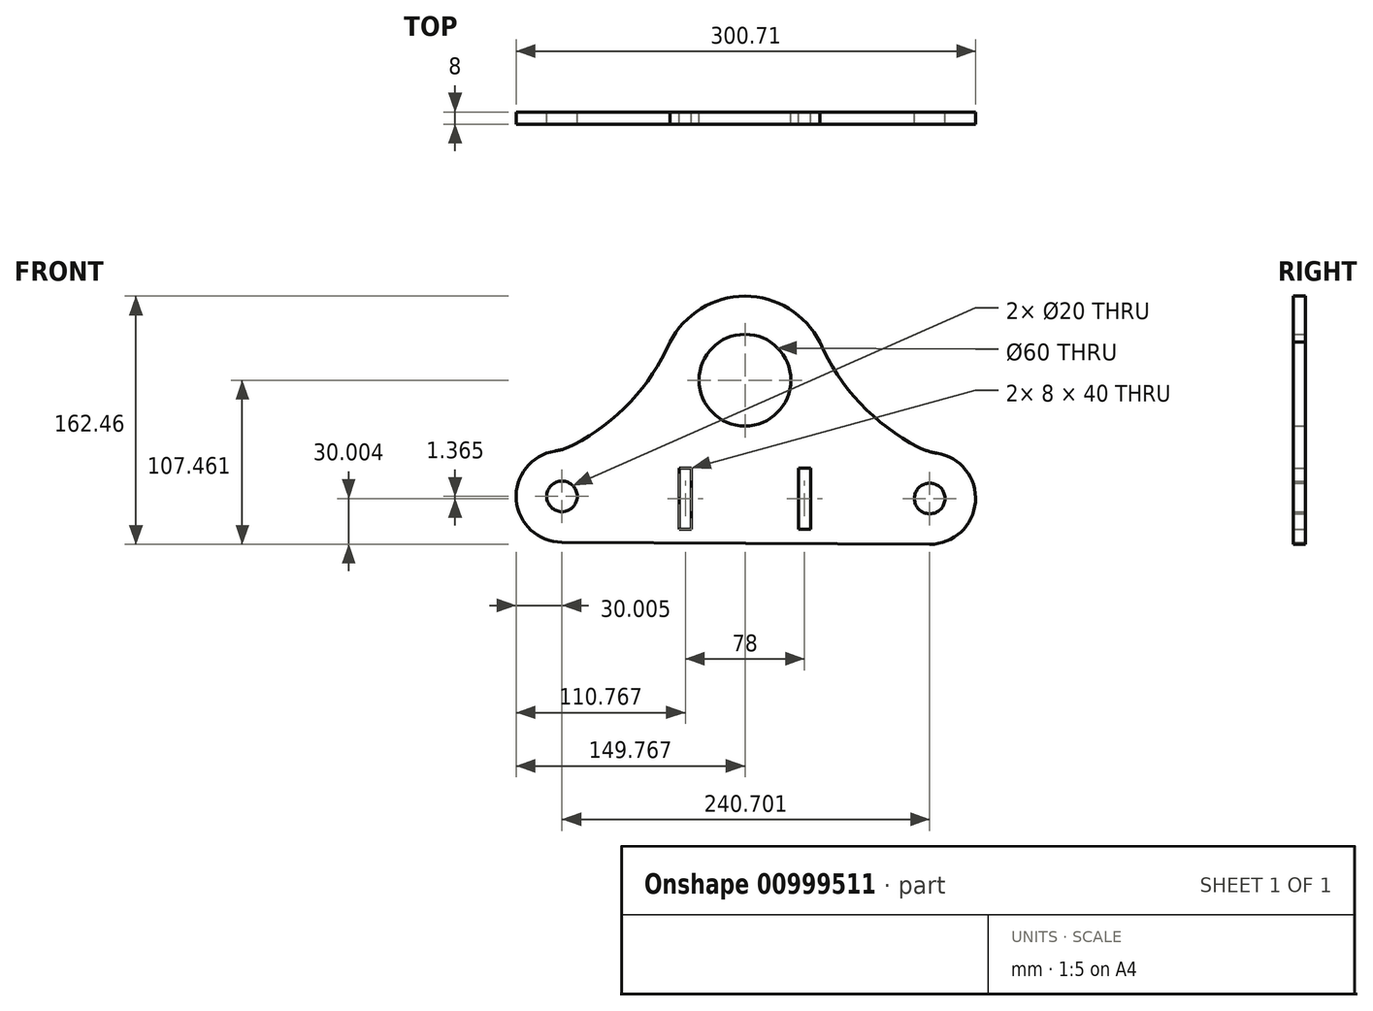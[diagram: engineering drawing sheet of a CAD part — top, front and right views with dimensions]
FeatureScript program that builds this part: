
annotation { "Feature Type Name" : "Feature", "Feature Type Description" : "" }
export const myFeature = defineFeature(function(context is Context, id is Id, definition is map)
    precondition{}
    {
        {
            var Q0;
            Q0=qCreatedBy(makeId("Front.planeOp"),FACE);
            var sketch = newSketch(context, id + "F0", { "sketchPlane" : qUnion([Q0])});
            skLineSegment(sketch, "E0", {"start": v(161.88, -50.78) * mm, "end": v(161.88, 59.22) * mm, "construction": true});
            skLineSegment(sketch, "E1", {"start": v(161.88, 59.22) * mm, "end": v(31.1, 109.22) * mm, "construction": true});
            skLineSegment(sketch, "E2", {"start": v(31.1, 109.22) * mm, "end": v(-27.49, 109.22) * mm, "construction": true});
            skLineSegment(sketch, "E3", {"start": v(-27.49, 109.22) * mm, "end": v(-158.83, 60.74) * mm, "construction": true});
            skLineSegment(sketch, "E4", {"start": v(-158.83, 60.74) * mm, "end": v(-158.83, -49.26) * mm, "construction": true});
            skCircle(sketch, "E5", {"center": v(0.94, 54.22) * mm, "radius": 30 * mm});
            skPoint(sketch, "E5.centerSnap0", {"position": v(0.94, -53.24) * mm});
            skCircle(sketch, "E6", {"center": v(121.88, -23.24) * mm, "radius": 10 * mm});
            skCircle(sketch, "E7", {"center": v(-118.83, -21.87) * mm, "radius": 10 * mm});
            skLineSegment(sketch, "E8.bottom", {"start": v(43.94, -3.24) * mm, "end": v(35.94, -3.24) * mm});
            skLineSegment(sketch, "E8.top", {"start": v(43.94, -43.24) * mm, "end": v(35.94, -43.24) * mm});
            skLineSegment(sketch, "E8.left", {"start": v(43.94, -3.24) * mm, "end": v(43.94, -43.24) * mm});
            skLineSegment(sketch, "E8.right", {"start": v(35.94, -3.24) * mm, "end": v(35.94, -43.24) * mm});
            skLineSegment(sketch, "E9.bottom", {"start": v(-34.06, -3.24) * mm, "end": v(-42.06, -3.24) * mm});
            skLineSegment(sketch, "E9.top", {"start": v(-34.06, -43.24) * mm, "end": v(-42.06, -43.24) * mm});
            skLineSegment(sketch, "E9.left", {"start": v(-34.06, -3.24) * mm, "end": v(-34.06, -43.24) * mm});
            skLineSegment(sketch, "E9.right", {"start": v(-42.06, -3.24) * mm, "end": v(-42.06, -43.24) * mm});
            skCircle(sketch, "E10", {"center": v(-118.83, -21.87) * mm, "radius": 30 * mm});
            skCircle(sketch, "E11", {"center": v(121.88, -23.24) * mm, "radius": 30 * mm});
            skCircle(sketch, "E12", {"center": v(0.94, 54.22) * mm, "radius": 55 * mm});
            skArc(sketch, "E13", {"start": v(-118.83, 8.13) * mm, "mid": v(-76.94, 37.04) * mm, "end": v(-48.15, 79.02) * mm});
            skArc(sketch, "E14", {"start": v(50.03, 79.02) * mm, "mid": v(79.14, 36.12) * mm, "end": v(121.88, 6.76) * mm});
            skLineSegment(sketch, "E15", {"start": v(-118.83, -51.87) * mm, "end": v(121.88, -53.24) * mm});
            skSolve(sketch);
        }
        {
            var Q0;
            Q0=makeQuery(id+"F0.imprint","IMPRINT",FACE,{"disambiguationData":[TD([[makeQuery(id+"F0.imprint","IMPRINT",EDGE,{"derivedFrom":sQuery(id+"F0.wireOp",EDGE,"E7")}),-1.0]])]});
            var Q1;
            Q1=makeQuery(id+"F0.imprint","IMPRINT",FACE,{"disambiguationData":[TD([[makeQuery(id+"F0.imprint","IMPRINT",EDGE,{"derivedFrom":sQuery(id+"F0.wireOp",EDGE,"E8.bottom")}),-1.0]])]});
            var Q2;
            Q2=makeQuery(id+"F0.imprint","IMPRINT",FACE,{"disambiguationData":[TD([[makeQuery(id+"F0.imprint","IMPRINT",EDGE,{"derivedFrom":sQuery(id+"F0.wireOp",EDGE,"E5")}),-1.0]])]});
            var Q3;
            Q3=makeQuery(id+"F0.imprint","IMPRINT",FACE,{"disambiguationData":[TD([[makeQuery(id+"F0.imprint","IMPRINT",EDGE,{"derivedFrom":sQuery(id+"F0.wireOp",EDGE,"E6")}),-1.0]])]});
            extrude(context, id + "F1", {"entities" : qUnion([Q0, Q1, Q2, Q3]), "depth" : 8 * mm, "offsetDistance" : 25 * mm});
        }
        {
            var Q0;
            Q0=makeQuery(id+"F1.opExtrude","SWEPT_EDGE",EDGE,{"disambiguationData":[OSD([sQuery(id+"F0.wireOp",EDGE,"E10"),sQuery(id+"F0.wireOp",EDGE,"E13")])]});
            var Q1;
            Q1=makeQuery(id+"F1.opExtrude","SWEPT_EDGE",EDGE,{"disambiguationData":[OSD([sQuery(id+"F0.wireOp",EDGE,"E11"),sQuery(id+"F0.wireOp",EDGE,"E14")])]});
            fillet(context, id + "F2", {"entities" : qUnion([Q0, Q1]), "tangentPropagation" : true, "radius" : 40 * mm, "defaultsChanged" : true, "vertexSettings" : [], "allowEdgeOverflow" : false});
        }
    });
